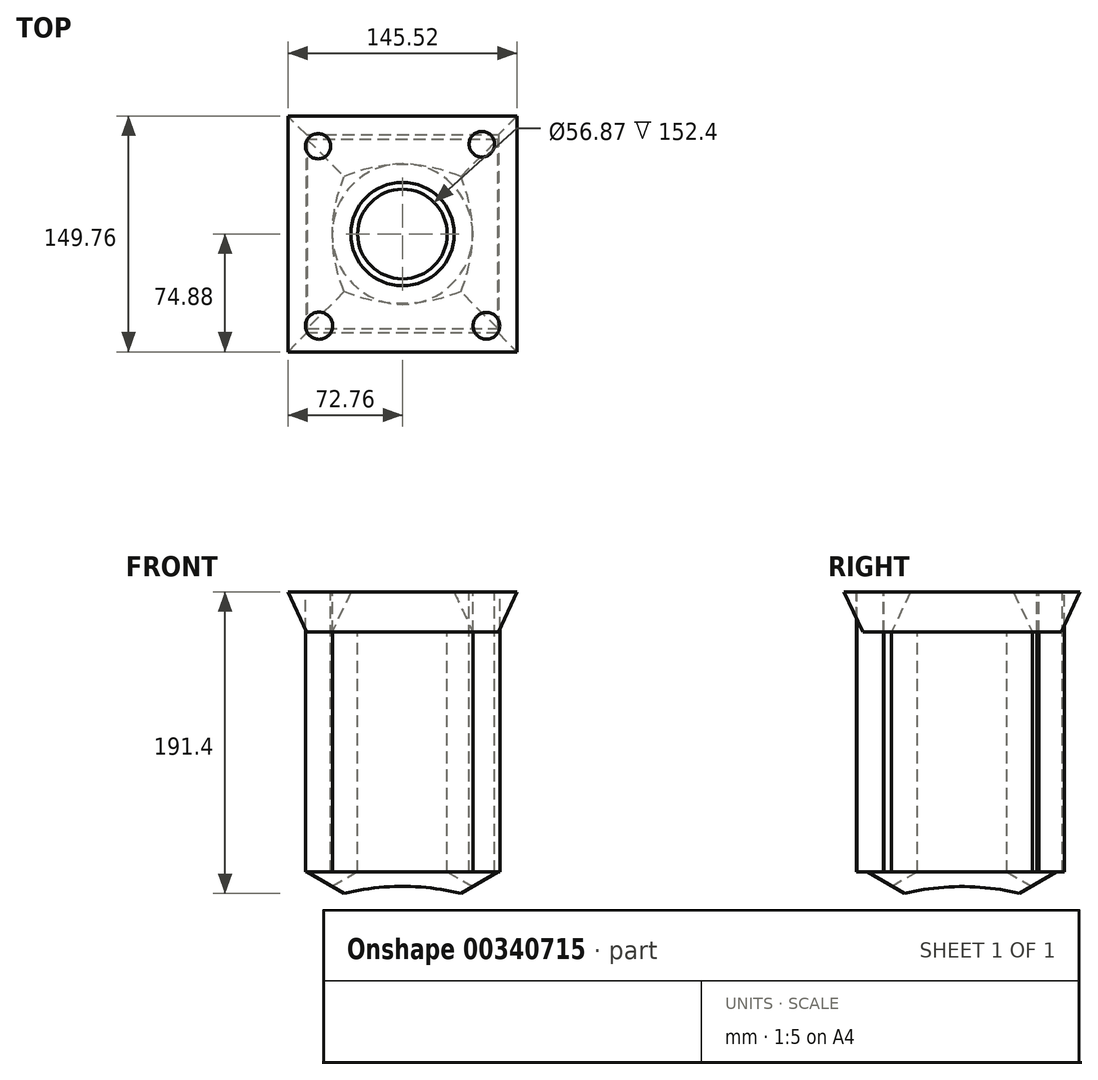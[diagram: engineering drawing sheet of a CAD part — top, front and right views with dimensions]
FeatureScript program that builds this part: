
annotation { "Feature Type Name" : "Feature", "Feature Type Description" : "" }
export const myFeature = defineFeature(function(context is Context, id is Id, definition is map)
    precondition{}
    {
        {
            var Q0;
            Q0=qCreatedBy(makeId("Top.planeOp"),FACE);
            var sketch = newSketch(context, id + "F0", { "sketchPlane" : qUnion([Q0])});
            skCircle(sketch, "E0", {"center": v(0, 0) * mm, "radius": 44.64 * mm});
            skSolve(sketch);
        }
        {
            var Q0;
            Q0=makeQuery(id+"F0.imprint","IMPRINT",FACE,{"disambiguationData":[TD([[makeQuery(id+"F0.imprint","IMPRINT",EDGE,{"derivedFrom":sQuery(id+"F0.wireOp",EDGE,"E0")}),1.0]])]});
            extrude(context, id + "F1", {"entities" : qUnion([Q0]), "depth" : 76.2 * mm, "hasSecondDirection" : true, "secondDirectionOppositeDirection" : true, "secondDirectionDepth" : 76.2 * mm});
        }
        {
            var Q0;
            Q0=makeQuery(id+"F1.opExtrude","CAP_FACE",FACE,{"disambiguationData":[OSD([sQuery(id+"F0.wireOp",EDGE,"E0")])],"isStart":false});
            var sketch = newSketch(context, id + "F2", { "sketchPlane" : qUnion([Q0])});
            skLineSegment(sketch, "E1.bottom", {"start": v(-60.92, 63.03) * mm, "end": v(60.92, 63.03) * mm});
            skLineSegment(sketch, "E1.top", {"start": v(-60.92, -63.03) * mm, "end": v(60.92, -63.03) * mm});
            skLineSegment(sketch, "E1.left", {"start": v(-60.92, 63.03) * mm, "end": v(-60.92, -63.03) * mm});
            skLineSegment(sketch, "E1.right", {"start": v(60.92, 63.03) * mm, "end": v(60.92, -63.03) * mm});
            skPoint(sketch, "E1.middle", {"position": v(0, 0) * mm});
            skSolve(sketch);
        }
        {
            var Q0;
            Q0=makeQuery(id+"F2.imprint","IMPRINT",FACE,{"disambiguationData":[TD([[makeQuery(id+"F2.imprint","IMPRINT",EDGE,{"derivedFrom":sQuery(id+"F2.wireOp",EDGE,"E1.bottom")}),-1.0]])]});
            extrude(context, id + "F3", {"entities" : qUnion([Q0]), "depth" : 25.4 * mm, "hasDraft" : true, "draftAngle" : 25 * degree});
        }
        {
            var Q0;
            Q0=makeQuery(id+"F1.opExtrude","CAP_FACE",FACE,{"disambiguationData":[OSD([sQuery(id+"F0.wireOp",EDGE,"E0")])],"isStart":false});
            var sketch = newSketch(context, id + "F4", { "sketchPlane" : qUnion([Q0])});
            skCircle(sketch, "E2", {"center": v(0, 0) * mm, "radius": 28.44 * mm});
            skSolve(sketch);
        }
        {
            var Q0;
            Q0=makeQuery(id+"F4.imprint","IMPRINT",FACE,{"disambiguationData":[TD([[makeQuery(id+"F4.imprint","IMPRINT",EDGE,{"derivedFrom":sQuery(id+"F4.wireOp",EDGE,"E2")}),1.0]])]});
            extrude(context, id + "F5", {"entities" : qUnion([Q0]), "operationType" : NewBodyOperationType.REMOVE, "oppositeDirection" : true, "depth" : 152.4 * mm});
        }
        {
            var Q0;
            Q0=makeQuery(id+"F1.opExtrude","CAP_FACE",FACE,{"disambiguationData":[OSD([sQuery(id+"F0.wireOp",EDGE,"E0")])],"isStart":true});
            var sketch = newSketch(context, id + "F6", { "sketchPlane" : qUnion([Q0])});
            skLineSegment(sketch, "E3.bottom", {"start": v(60.6, 60.08) * mm, "end": v(-60.6, 60.08) * mm});
            skLineSegment(sketch, "E3.top", {"start": v(60.6, -60.08) * mm, "end": v(-60.6, -60.08) * mm});
            skLineSegment(sketch, "E3.left", {"start": v(60.6, 60.08) * mm, "end": v(60.6, -60.08) * mm});
            skLineSegment(sketch, "E3.right", {"start": v(-60.6, 60.08) * mm, "end": v(-60.6, -60.08) * mm});
            skPoint(sketch, "E3.middle", {"position": v(0, 0) * mm});
            skSolve(sketch);
        }
        {
            var Q0;
            Q0=makeQuery(id+"F6.imprint","IMPRINT",FACE,{"disambiguationData":[TD([[makeQuery(id+"F6.imprint","IMPRINT",EDGE,{"derivedFrom":makeQuery(id+"F1.opExtrude","CAP_EDGE",EDGE,{"disambiguationData":[OSD([sQuery(id+"F0.wireOp",EDGE,"E0")])],"isStart":true})}),-1.0]])]});
            var Q1;
            Q1=makeQuery(id+"F6.imprint","IMPRINT",FACE,{"disambiguationData":[TD([[makeQuery(id+"F6.imprint","IMPRINT",EDGE,{"derivedFrom":sQuery(id+"F6.wireOp",EDGE,"E3.bottom")}),1.0]])]});
            var Q2;
            Q2=makeQuery(id+"F6.imprint","IMPRINT",FACE,{"disambiguationData":[TD([[makeQuery(id+"F6.imprint","IMPRINT",EDGE,{"derivedFrom":makeQuery(id+"F5.boolean.opBoolean","COPY",EDGE,{"derivedFrom":makeQuery(id+"F5.opExtrude","CAP_EDGE",EDGE,{"disambiguationData":[OSD([sQuery(id+"F4.wireOp",EDGE,"E2")])],"isStart":false})})}),-1.0]])]});
            extrude(context, id + "F7", {"entities" : qUnion([Q0, Q1, Q2]), "operationType" : NewBodyOperationType.ADD, "depth" : 50.8 * mm, "hasDraft" : true, "draftAngle" : 60 * degree, "draftPullDirection" : true});
        }
        {
            var Q0;
            Q0=makeQuery(id+"F3.opExtrude","CAP_FACE",FACE,{"disambiguationData":[OSD([sQuery(id+"F0.wireOp",EDGE,"E0"),sQuery(id+"F2.wireOp",EDGE,"E1.bottom"),sQuery(id+"F2.wireOp",EDGE,"E1.top"),sQuery(id+"F2.wireOp",EDGE,"E1.left"),sQuery(id+"F2.wireOp",EDGE,"E1.right")])],"isStart":false});
            var sketch = newSketch(context, id + "F8", { "sketchPlane" : qUnion([Q0])});
            skCircle(sketch, "E4", {"center": v(-53.6, 55.77) * mm, "radius": 8.02 * mm});
            skCircle(sketch, "E5", {"center": v(-52.98, -58.25) * mm, "radius": 8.64 * mm});
            skCircle(sketch, "E6", {"center": v(50.4, 57.07) * mm, "radius": 8.12 * mm});
            skCircle(sketch, "E7", {"center": v(53.32, -58.28) * mm, "radius": 8.5 * mm});
            skSolve(sketch);
        }
        {
            var Q0;
            Q0=makeQuery(id+"F8.imprint","IMPRINT",FACE,{"disambiguationData":[TD([[makeQuery(id+"F8.imprint","IMPRINT",EDGE,{"derivedFrom":sQuery(id+"F8.wireOp",EDGE,"E7")}),1.0]])]});
            var Q1;
            Q1=makeQuery(id+"F8.imprint","IMPRINT",FACE,{"disambiguationData":[TD([[makeQuery(id+"F8.imprint","IMPRINT",EDGE,{"derivedFrom":sQuery(id+"F8.wireOp",EDGE,"E6")}),1.0]])]});
            var Q2;
            Q2=makeQuery(id+"F8.imprint","IMPRINT",FACE,{"disambiguationData":[TD([[makeQuery(id+"F8.imprint","IMPRINT",EDGE,{"derivedFrom":sQuery(id+"F8.wireOp",EDGE,"E4")}),1.0]])]});
            var Q3;
            Q3=makeQuery(id+"F8.imprint","IMPRINT",FACE,{"disambiguationData":[TD([[makeQuery(id+"F8.imprint","IMPRINT",EDGE,{"derivedFrom":sQuery(id+"F8.wireOp",EDGE,"E5")}),1.0]])]});
            extrude(context, id + "F9", {"entities" : qUnion([Q0, Q1, Q2, Q3]), "oppositeDirection" : true, "depth" : 177.8 * mm});
        }
    });
